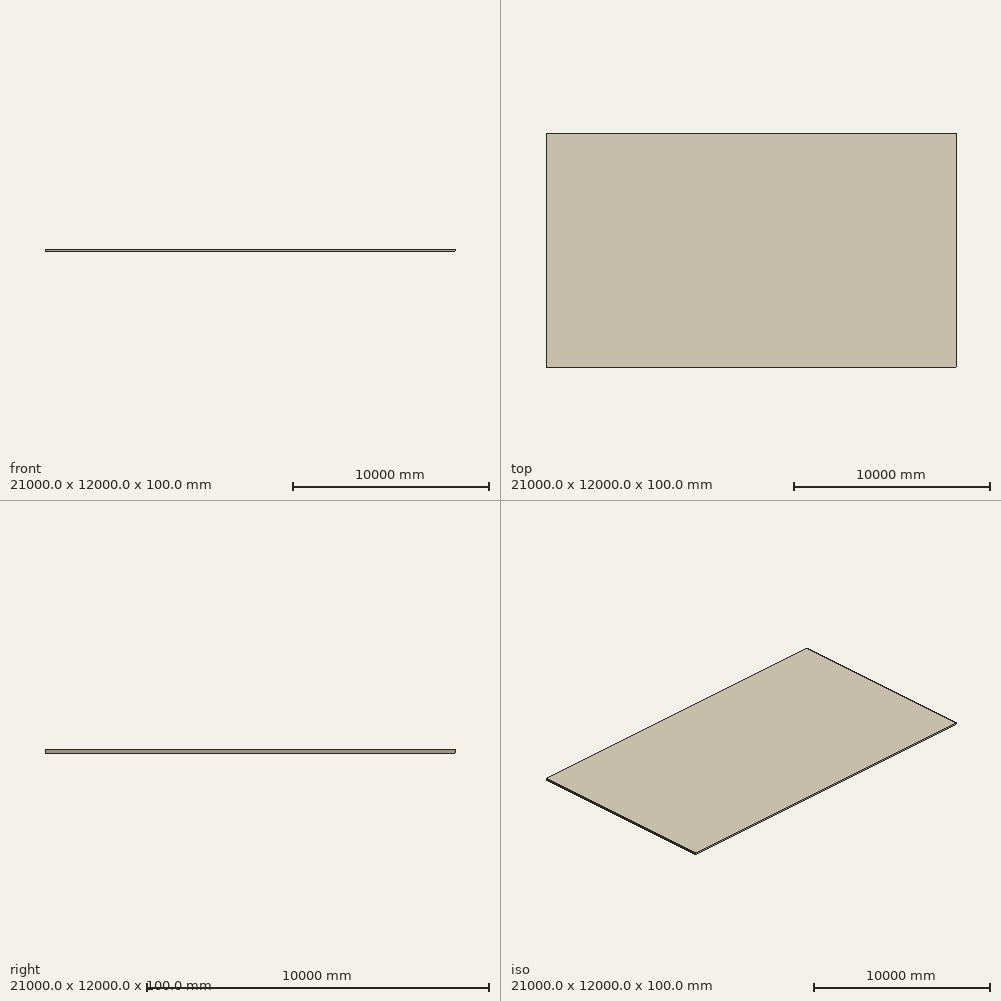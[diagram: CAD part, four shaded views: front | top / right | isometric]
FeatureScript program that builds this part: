
annotation { "Feature Type Name" : "Feature", "Feature Type Description" : "" }
export const myFeature = defineFeature(function(context is Context, id is Id, definition is map)
    precondition{}
    {
        {
            var Q0;
            Q0=qCreatedBy(makeId("Top.planeOp"),FACE);
            var sketch = newSketch(context, id + "F0", { "sketchPlane" : qUnion([Q0])});
            skLineSegment(sketch, "E0.bottom", {"start": v(-10500, 6000) * mm, "end": v(10500, 6000) * mm});
            skLineSegment(sketch, "E0.top", {"start": v(-10500, -6000) * mm, "end": v(10500, -6000) * mm});
            skLineSegment(sketch, "E0.left", {"start": v(-10500, 6000) * mm, "end": v(-10500, -6000) * mm});
            skLineSegment(sketch, "E0.right", {"start": v(10500, 6000) * mm, "end": v(10500, -6000) * mm});
            skPoint(sketch, "E0.middle", {"position": v(0, 0) * mm});
            skSolve(sketch);
        }
        {
            var Q0;
            Q0=makeQuery(id+"F0.imprint","IMPRINT",FACE,{"disambiguationData":[TD([[makeQuery(id+"F0.imprint","IMPRINT",EDGE,{"derivedFrom":sQuery(id+"F0.wireOp",EDGE,"E0.bottom")}),-1.0]])]});
            extrude(context, id + "F1", {"entities" : qUnion([Q0]), "oppositeDirection" : true, "depth" : 100 * mm, "offsetDistance" : 25 * mm});
        }
    });
